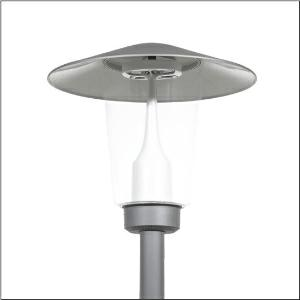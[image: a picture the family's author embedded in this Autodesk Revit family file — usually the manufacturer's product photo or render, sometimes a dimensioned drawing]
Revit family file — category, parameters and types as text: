
# Revit family: pilzleuchte_iq___st1_2a_5xa5235ef14hp_2efb
name_source: partatom
category: Lighting Fixtures
units: mm (PartAtom-declared; Revit-internal decimal feet)

## family parameters
Cut with Voids When Loaded = No
Host = Face
Light Source = No
Part Type = Normal
Room Calculation Point = No
Round Connector Dimension = Use Diameter
Shared = No

## types (1)
- --- (1 x LED, 4770 lm, 33.6 W, 3000K)
    Apparent Load = 34 VA
    CIE Flux Codes = 23 60 92 98 100
    Color Rendering = 70
    Color Temperature = 3000K
    Default Elevation = 1800 mm
    Description = Mushroom Luminaire iQ, mast luminaire, Module 540 iQ-SR, primary light control with 3 zone facetted reflector, of plastic, silver coated, highly specular, structured, primary optical cover: cover, of PMMA, transparent, light distribution: ST1.2a, light emission: direct distribution, primary light characteristic: asymmetric, installation type: post-top, LED, High Power LED, rated luminous flux: 4.770lm, luminous efficacy: 142lm/W, light colour: 730, colour temperature: 3000K, control gear: iQ Street-Remote, control: pre-setting: logarithmic dimming characteristic, Street-Remote, Auto-Match, Temp-Guard, Lumen-Switch, Night-Set, Smart-Wire, Light-Fading, Desk-Remote (wireless, voltage-free reading and setting of iQ features in the workshop via application-optimized NFC function/RFID function), optimised constant luminous flux control (CLO 2.0), with terminal, 6-pole, max. 2.5mm², mains connection: 230..240V, AC, 50/60Hz, start of lifetime: 34W, end of service life: 36W, reduction: 15W, luminaire housing, upper part, of glass-fibre reinforced polyester, coated, Siteco® metallic grey (DB 702S), diameter: 650mm, height: 586mm, spigot size: d x l = 76 x 70mm (post-top) | with reducer (optional accessory) 60 x 70mm, mounting height: 3..5m, post-top mast mounting element, of diecast aluminium, coated, Siteco® metallic grey (DB 702S), Module 540 iQ-SR, traffic white (RAL 9016), equipment: Power, protection rating (complete): IP65, insulation class (complete): insulation class II (safety insulation), certification: CE, ENEC, VDE, packaging unit: 1 piece

Light Distribution: ST1.2a
    Height = 586 mm
    Lamp = 1 x LED
    Lamp Light Flux = 4770 lm
    Lamp Power = 33.6 W
    Lamp count = 1
    Length = 650 mm
    Luminous efficacy = 142 lm/W
    Manufacturer = Siteco
    ModVariant = No
    Model = 5XA5235EF14HP
    Mounting Place = Pole
    Mounting Type = Pole top
    Number of Poles = 1
    OnlyDefault = Yes
    Power Factor = 1
    Product Name = Pilzleuchte iQ | ST1.2a
    Product group = mast luminaire | pylon top
    ProductGroupID = 6100
    Protection Class = Protection class II
    Protection Degree = IP 65
    RLX_Detail_Level = 1
    RLX_Emergency_Light_Flux = 0 lm
    RLX_Emergency_Type = 0
    RLX_Emergency_Type_DB = No
    RlxData = <blob elided: 51577 chars, md5=67398748>
    Socket = socket
    Standby Power = 0 W
    System Light Flux = 4770 lm
    System Power = 34 W
    Type Comments = factory setting: luminous flux: 100 % | dim-lin: 254 | 695 mA
    Type Image = l_1006077.jpg
    URL = http://relux.com
    VarID = @adj_192641
    Voltage = 0 V
    Weight = 0.00 kg
    Width = 0 mm  [stored 0 ft]

note: [stored X ft] marks values corroborated as IEEE doubles in the binary element streams (Revit-internal decimal feet)

## geometry (parser evidence)
native form markers: Blend x4, Sweep x11
no freeform markers — native parametric forms only
